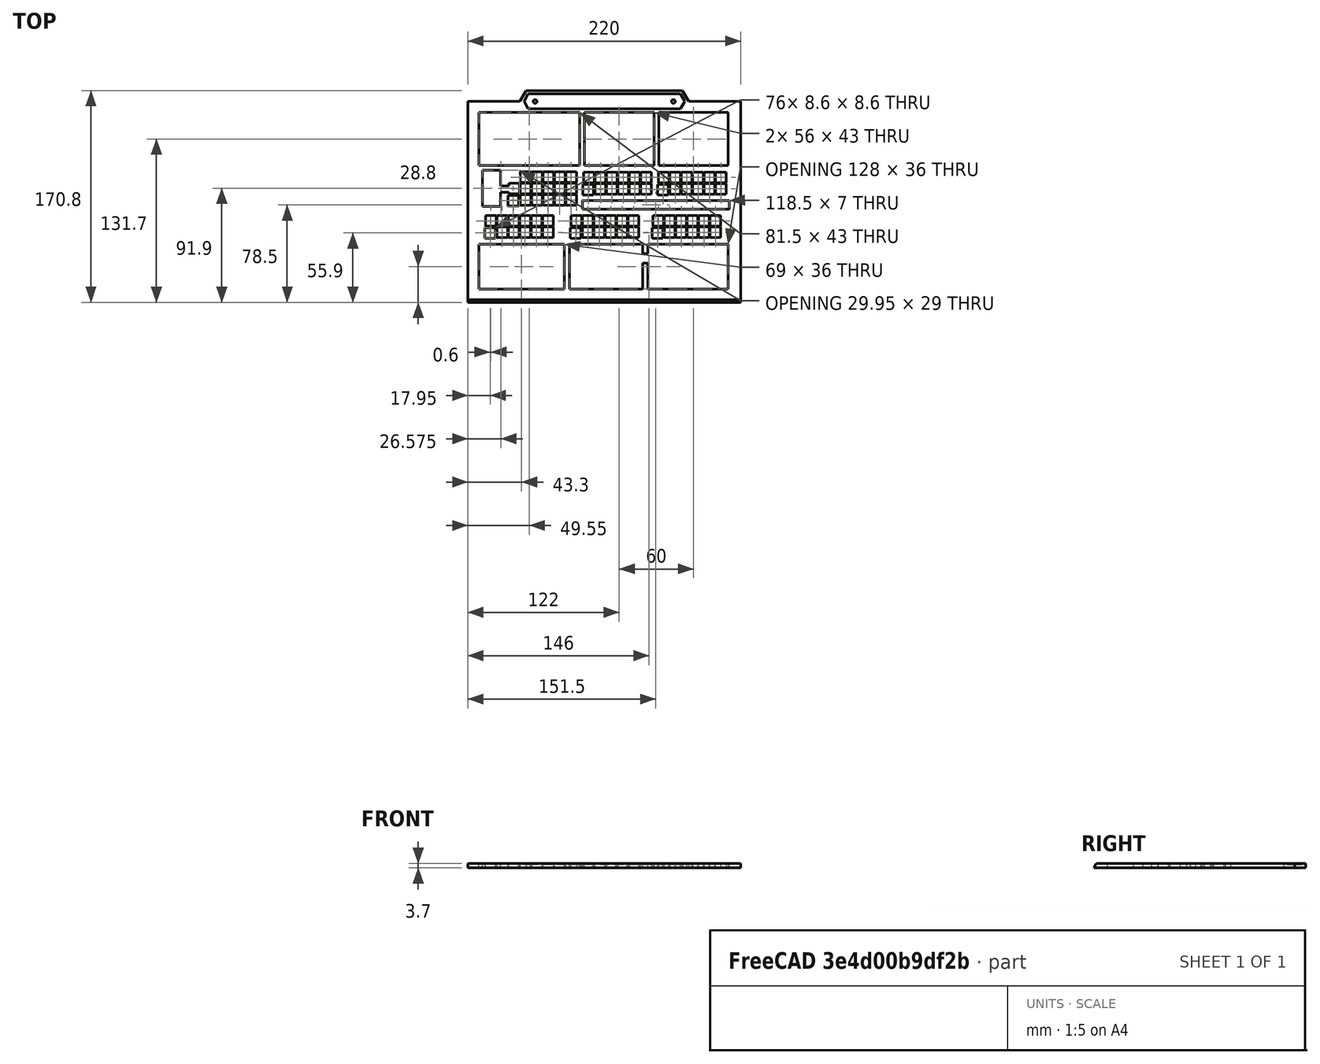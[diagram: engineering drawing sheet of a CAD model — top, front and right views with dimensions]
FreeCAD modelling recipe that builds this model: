
FCSTD DOCUMENT  (FreeCAD 0.21R33668 +26 (Git))
Label: overlay-full-v1
License: All rights reserved
LicenseURL: https://en.wikipedia.org/wiki/All_rights_reserved
objects: Sketcher::SketchObject×5, PartDesign::Pad×4, Part::Feature×2, PartDesign::Pocket×2, Mesh::Feature×1, Part::Refine×1, PartDesign::FeatureBase×1, Part::Part2DObjectPython×1, PartDesign::Body×1
note: 23 computed .brp shape members not serialized (recipe doc carries the construction recipe); baked Part::Feature solids carry a one-line shape summary decoded from their .brp

FEATURE [Mesh::Feature] Terraforming_Mars_overlay
FEATURE [Part::Feature] Terraforming_Mars_overlay001
  shape: bbox 208 x 148 x 3.7 mm, 1736 faces, 0 solids (baked)
FEATURE [Part::Feature] Terraforming_Mars_overlay001_solid  label="Terraforming_Mars_overlay001 (Solid)"
  shape: bbox 208 x 148 x 3.7 mm, 1736 faces (baked)
FEATURE [Part::Refine] Terraforming_Mars_overlay001_solid001  label="Terraforming_Mars_overlay001 (Solid)001"
  Source = -> Terraforming_Mars_overlay001_solid
FEATURE [PartDesign::FeatureBase] BaseFeature
  BaseFeature = -> Terraforming_Mars_overlay001_solid001
FEATURE [Sketcher::SketchObject] Sketch
  ExternalGeometry = -> [BaseFeature]
  FullyConstrained = true
  MapMode = 5
  Placement = pos=(0,0,3.7) rot=(0,0,1;0rad)
  Support = -> [BaseFeature]
  sketch-geometry (8):
    g0: LineSegment StartX=6 StartY=154 StartZ=0 EndX=214 EndY=154 EndZ=0
    g1: LineSegment StartX=214 StartY=154 StartZ=0 EndX=214 EndY=6 EndZ=0
    g2: LineSegment StartX=214 StartY=6 StartZ=0 EndX=6 EndY=6 EndZ=0
    g3: LineSegment StartX=6 StartY=6 StartZ=0 EndX=6 EndY=154 EndZ=0
    g4: LineSegment StartX=0 StartY=160 StartZ=0 EndX=220 EndY=160 EndZ=0
    g5: LineSegment StartX=220 StartY=160 StartZ=0 EndX=220 EndY=0 EndZ=0
    g6: LineSegment StartX=220 StartY=0 StartZ=0 EndX=0 EndY=0 EndZ=0
    g7: LineSegment StartX=0 StartY=0 StartZ=0 EndX=0 EndY=160 EndZ=0
  constraints (22):
    c: Coincident(g0,g1)
    c: Coincident(g1,g2)
    c: Coincident(g2,g3)
    c: Coincident(g3,g0)
    c: Horizontal(g0)
    c: Horizontal(g2)
    c: Vertical(g1)
    c: Vertical(g3)
    c: Coincident(g0,g-3)
    c: Coincident(g1,g-4)
    c: Coincident(g4,g5)
    c: Coincident(g5,g6)
    c: Coincident(g6,g7)
    c: Coincident(g7,g4)
    c: Horizontal(g4)
    c: Horizontal(g6)
    c: Vertical(g5)
    c: Vertical(g7)
    c: DistanceX(g4,g0) = 6
    c: DistanceX(g0,g4) = 6
    c: DistanceY(g0,g4) = 6
    c: DistanceY(g5,g1) = 6
FEATURE [PartDesign::Pad] Pad
  BaseFeature = -> BaseFeature
  Direction = (0,0,1)
  Length = 10
  Length2 = 10
  Profile = -> Sketch
  ReferenceAxis = -> Sketch [N_Axis]
  Type = 3
  UpToFace = -> BaseFeature [Face1]
FEATURE [Sketcher::SketchObject] Sketch001
  ExternalGeometry = -> [Pad]
  FullyConstrained = true
  MapMode = 5
  Placement = pos=(0,0,3.7) rot=(0,0,1;0rad)
  Support = -> [Pad]
  sketch-geometry (5):
    g0: GeomPoint X=110 Y=160 Z=0
    g1: LineSegment StartX=42 StartY=160 StartZ=0 EndX=47.0807 EndY=168.8 EndZ=0
    g2: LineSegment StartX=47.0807 StartY=168.8 StartZ=0 EndX=172.919 EndY=168.8 EndZ=0
    g3: LineSegment StartX=172.919 StartY=168.8 StartZ=0 EndX=178 EndY=160 EndZ=0
    g4: LineSegment StartX=178 StartY=160 StartZ=0 EndX=42 EndY=160 EndZ=0
  constraints (13):
    c: Symmetric(g-3,g-3,g0)
    c: Coincident(g1,g2)
    c: Horizontal(g2)
    c: Coincident(g2,g3)
    c: Coincident(g3,g4)
    c: Coincident(g4,g1)
    c: Angle(g1,g4,g1) = 2.0944
    c: Angle(g4,g3,g3) = 2.0944
    c: DistanceY(g1,g1) = 8.8
    c: PointOnObject(g1,g-3)
    c: DistanceX(g-3,g1) = 42
    c: DistanceX(g3,g-3) = 42
    c: PointOnObject(g3,g-3)
FEATURE [PartDesign::Pad] Pad001
  BaseFeature = -> Pad
  Direction = (0,0,1)
  Length = 10
  Length2 = 10
  Profile = -> Sketch001
  ReferenceAxis = -> Sketch001 [N_Axis]
  Type = 3
  UpToFace = -> Pad [Face2]
FEATURE [Sketcher::SketchObject] Sketch002
  ExternalGeometry = -> [Pad001]
  FullyConstrained = true
  MapMode = 5
  Placement = pos=(0,0,3.7) rot=(0,0,1;0rad)
  Support = -> [Pad001]
  sketch-geometry (7):
    g0: GeomPoint X=110 Y=160 Z=0
    g1: LineSegment StartX=45.2332 StartY=160 StartZ=0 EndX=48.6973 EndY=166 EndZ=0
    g2: LineSegment StartX=48.6973 StartY=166 StartZ=0 EndX=171.303 EndY=166 EndZ=0
    g3: LineSegment StartX=171.303 StartY=166 StartZ=0 EndX=174.767 EndY=160 EndZ=0
    g4: LineSegment StartX=174.767 StartY=160 StartZ=0 EndX=171.303 EndY=154 EndZ=0
    g5: LineSegment StartX=171.303 StartY=154 StartZ=0 EndX=48.6973 EndY=154 EndZ=0
    g6: LineSegment StartX=48.6973 StartY=154 StartZ=0 EndX=45.2332 EndY=160 EndZ=0
  constraints (17):
    c: Symmetric(g-4,g-4,g0)
    c: PointOnObject(g1,g-4)
    c: Coincident(g1,g2)
    c: Horizontal(g2)
    c: Coincident(g2,g3)
    c: PointOnObject(g3,g-4)
    c: Coincident(g3,g4)
    c: PointOnObject(g4,g-5)
    c: Coincident(g4,g5)
    c: Coincident(g5,g6)
    c: Coincident(g6,g1)
    c: Parallel(g1,g-6)
    c: Symmetric(g5,g1,g-4)
    c: Symmetric(g4,g2,g-4)
    c: Parallel(g3,g-7)
    c: Distance(g1,g-6) = 2.8
    c: Distance(g2,g-7) = 2.8
FEATURE [PartDesign::Pocket] Pocket
  BaseFeature = -> Pad001
  Direction = (0,0,-1)
  Length = 1
  Length2 = 5
  Profile = -> Sketch002
  ReferenceAxis = -> Sketch002 [N_Axis]
  Type = 0
FEATURE [Part::Part2DObjectPython] ShapeString  # Draft 2D object (typed FeaturePython)
  FontFile = <path>
  MakeFace = true
  Placement = pos=(61.7,155.5,2.7) rot=(0,0,1;0rad)
  Size = 9
  String = TERRAFORMING MARS
  Tracking = 0
FEATURE [Sketcher::SketchObject] Sketch003
  ExternalGeometry = -> [Pocket]
  FullyConstrained = true
  MapMode = 5
  Placement = pos=(0,0,2.7) rot=(0,0,1;0rad)
  Support = -> [Pocket]
  sketch-geometry (3):
    g0: LineSegment StartX=45.2332 StartY=160 StartZ=0 EndX=174.767 EndY=160 EndZ=0
    g1: Circle CenterX=54.2332 CenterY=160 CenterZ=0 NormalX=0 NormalY=0 NormalZ=1 AngleXU=0 Radius=1.5
    g2: Circle CenterX=165.767 CenterY=160 CenterZ=0 NormalX=0 NormalY=0 NormalZ=1 AngleXU=0 Radius=1.5
  constraints (8):
    c: Coincident(g0,g-3)
    c: Coincident(g0,g-4)
    c: PointOnObject(g1,g0)
    c: PointOnObject(g2,g0)
    c: Diameter(g2) = 3
    c: Diameter(g1) = 3
    c: DistanceX(g0,g1) = 9
    c: DistanceX(g2,g0) = 9
FEATURE [PartDesign::Pad] Pad002
  BaseFeature = -> Pocket
  Direction = (0,0,1)
  Length = 1
  Length2 = 10
  Profile = -> Sketch003
  ReferenceAxis = -> Sketch003 [N_Axis]
  Type = 0
FEATURE [PartDesign::Pad] Pad003
  BaseFeature = -> Pad002
  Direction = (0,-1,0)
  Length = 2
  Length2 = 10
  Profile = -> Pad002 [Face352]
  Type = 0
FEATURE [Sketcher::SketchObject] Sketch004
  ExternalGeometry = -> [Pad003]
  FullyConstrained = true
  MapMode = 5
  Placement = pos=(220,0,0) rot=(0.57735,0.57735,0.57735;2.0944rad)
  Support = -> [Pad003]
  sketch-geometry (3):
    g0: LineSegment StartX=0 StartY=3.7 StartZ=0 EndX=-2 EndY=0 EndZ=0
    g1: LineSegment StartX=-2 StartY=0 StartZ=0 EndX=-2 EndY=3.7 EndZ=0
    g2: LineSegment StartX=-2 StartY=3.7 StartZ=0 EndX=0 EndY=3.7 EndZ=0
  constraints (6):
    c: Coincident(g-4,g0)
    c: Coincident(g0,g-3)
    c: Coincident(g0,g1)
    c: Coincident(g1,g-4)
    c: Coincident(g1,g2)
    c: Coincident(g2,g0)
FEATURE [PartDesign::Pocket] Pocket001
  BaseFeature = -> Pad003
  Direction = (-1,0,0)
  Length = 5
  Length2 = 5
  Profile = -> Sketch004
  ReferenceAxis = -> Sketch004 [N_Axis]
  Type = 1
FEATURE [PartDesign::Body] Body
  BaseFeature = -> Terraforming_Mars_overlay001_solid001
  Group = -> [BaseFeature,Sketch,Pad,Sketch001,Pad001,Sketch002,Pocket,Sketch003,Pad002,Pad003,Sketch004,Pocket001]
  Origin = -> Origin
  Tip = -> Pocket001
note: 1 file-system path scrubbed to <path> (originals preserved in the JSON sidecar)
